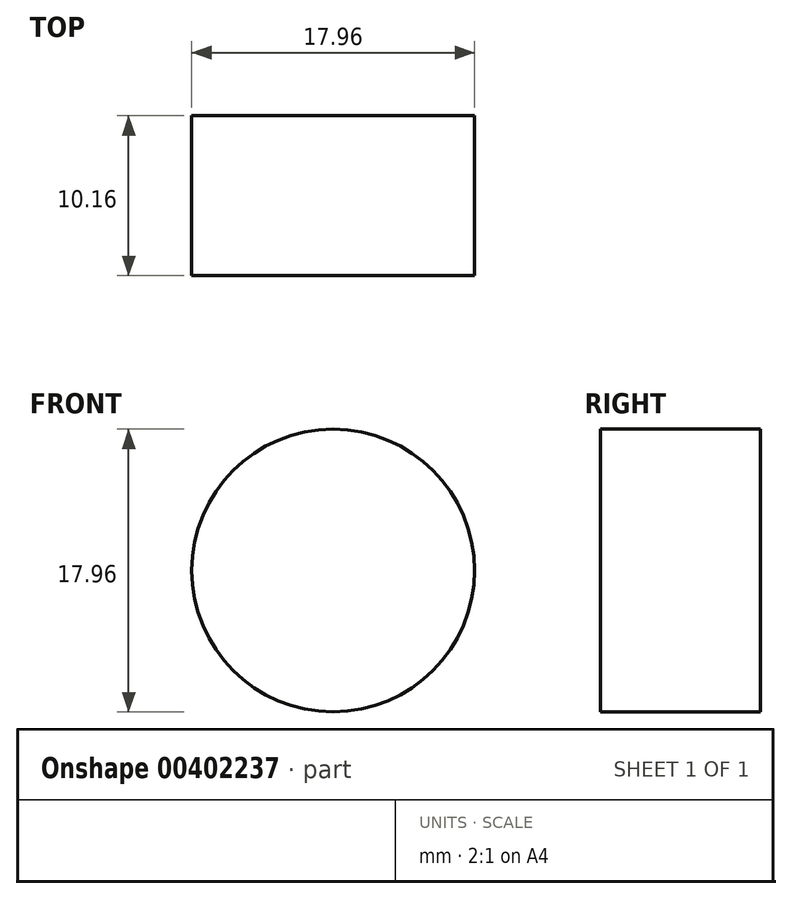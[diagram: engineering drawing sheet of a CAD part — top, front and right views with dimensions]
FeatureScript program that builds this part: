
annotation { "Feature Type Name" : "Feature", "Feature Type Description" : "" }
export const myFeature = defineFeature(function(context is Context, id is Id, definition is map)
    precondition{}
    {
        {
            var Q0;
            Q0=qCreatedBy(makeId("Front.planeOp"),FACE);
            var sketch = newSketch(context, id + "F0", { "sketchPlane" : qUnion([Q0])});
            skCircle(sketch, "E0", {"center": v(0, 0) * mm, "radius": 8.98 * mm});
            skSolve(sketch);
        }
        {
            var Q0;
            Q0=makeQuery(id+"F0.imprint","IMPRINT",FACE,{"disambiguationData":[TD([[makeQuery(id+"F0.imprint","IMPRINT",EDGE,{"derivedFrom":sQuery(id+"F0.wireOp",EDGE,"E0")}),1.0]])]});
            extrude(context, id + "F1", {"entities" : qUnion([Q0]), "depth" : 10.16 * mm});
        }
    });
